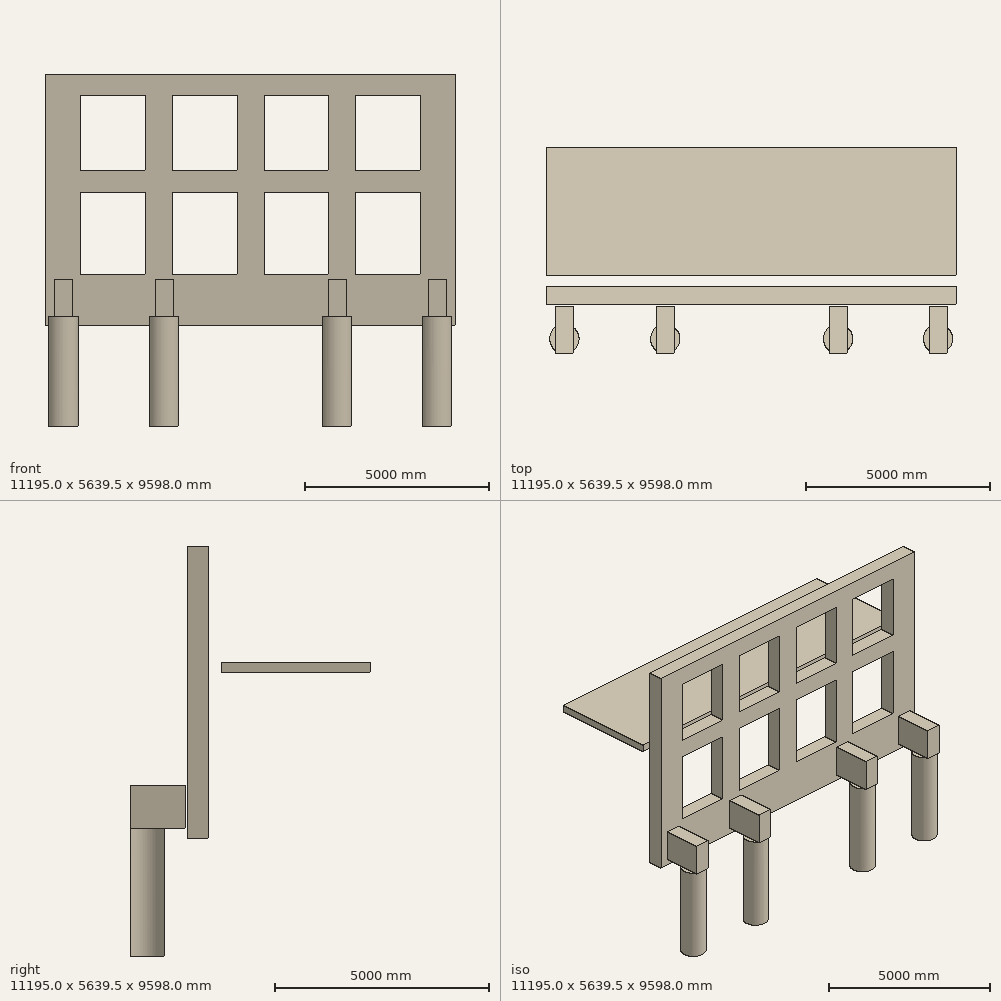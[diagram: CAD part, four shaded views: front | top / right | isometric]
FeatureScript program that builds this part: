
annotation { "Feature Type Name" : "Feature", "Feature Type Description" : "" }
export const myFeature = defineFeature(function(context is Context, id is Id, definition is map)
    precondition{}
    {
        {
            var Q0;
            Q0=qCreatedBy(makeId("Top.planeOp"),FACE);
            var sketch = newSketch(context, id + "F0", { "sketchPlane" : qUnion([Q0])});
            skLineSegment(sketch, "E0.bottom", {"start": v(2110, -40) * mm, "end": v(2610, -40) * mm});
            skLineSegment(sketch, "E0.top", {"start": v(2110, -1340) * mm, "end": v(2610, -1340) * mm});
            skLineSegment(sketch, "E0.left", {"start": v(2110, -40) * mm, "end": v(2110, -1340) * mm});
            skLineSegment(sketch, "E0.right", {"start": v(2610, -40) * mm, "end": v(2610, -1340) * mm});
            skLineSegment(sketch, "E1.bottom", {"start": v(4840, -40) * mm, "end": v(5340, -40) * mm});
            skLineSegment(sketch, "E1.top", {"start": v(4840, -1340) * mm, "end": v(5340, -1340) * mm});
            skLineSegment(sketch, "E1.left", {"start": v(4840, -40) * mm, "end": v(4840, -1340) * mm});
            skLineSegment(sketch, "E1.right", {"start": v(5340, -40) * mm, "end": v(5340, -1340) * mm});
            skLineSegment(sketch, "E2.bottom", {"start": v(-2110, -40) * mm, "end": v(-2610, -40) * mm});
            skLineSegment(sketch, "E2.top", {"start": v(-2110, -1340) * mm, "end": v(-2610, -1340) * mm});
            skLineSegment(sketch, "E2.left", {"start": v(-2110, -40) * mm, "end": v(-2110, -1340) * mm});
            skLineSegment(sketch, "E2.right", {"start": v(-2610, -40) * mm, "end": v(-2610, -1340) * mm});
            skLineSegment(sketch, "E3.bottom", {"start": v(-4865, -40) * mm, "end": v(-5365, -40) * mm});
            skLineSegment(sketch, "E3.top", {"start": v(-4865, -1340) * mm, "end": v(-5365, -1340) * mm});
            skLineSegment(sketch, "E3.left", {"start": v(-4865, -40) * mm, "end": v(-4865, -1340) * mm});
            skLineSegment(sketch, "E3.right", {"start": v(-5365, -40) * mm, "end": v(-5365, -1340) * mm});
            skSolve(sketch);
        }
        {
            var Q0;
            Q0=makeQuery(id+"F0.imprint","IMPRINT",FACE,{"disambiguationData":[TD([[makeQuery(id+"F0.imprint","IMPRINT",EDGE,{"derivedFrom":sQuery(id+"F0.wireOp",EDGE,"E3.bottom")}),1.0]])]});
            var Q1;
            Q1=makeQuery(id+"F0.imprint","IMPRINT",FACE,{"disambiguationData":[TD([[makeQuery(id+"F0.imprint","IMPRINT",EDGE,{"derivedFrom":sQuery(id+"F0.wireOp",EDGE,"E2.bottom")}),1.0]])]});
            var Q2;
            Q2=makeQuery(id+"F0.imprint","IMPRINT",FACE,{"disambiguationData":[TD([[makeQuery(id+"F0.imprint","IMPRINT",EDGE,{"derivedFrom":sQuery(id+"F0.wireOp",EDGE,"E0.bottom")}),-1.0]])]});
            var Q3;
            Q3=makeQuery(id+"F0.imprint","IMPRINT",FACE,{"disambiguationData":[TD([[makeQuery(id+"F0.imprint","IMPRINT",EDGE,{"derivedFrom":sQuery(id+"F0.wireOp",EDGE,"E1.bottom")}),-1.0]])]});
            extrude(context, id + "F1", {"entities" : qUnion([Q0, Q1, Q2, Q3]), "oppositeDirection" : true, "depth" : 1000 * mm});
        }
        {
            var Q0;
            Q0=makeQuery(id+"F1.opExtrude","CAP_FACE",FACE,{"disambiguationData":[OSD([sQuery(id+"F0.wireOp",EDGE,"E3.bottom"),sQuery(id+"F0.wireOp",EDGE,"E3.top"),sQuery(id+"F0.wireOp",EDGE,"E3.left"),sQuery(id+"F0.wireOp",EDGE,"E3.right")])],"isStart":false});
            var sketch = newSketch(context, id + "F2", { "sketchPlane" : qUnion([Q0])});
            skCircle(sketch, "E4", {"center": v(-5115, 940) * mm, "radius": 400 * mm});
            skPoint(sketch, "E4.centerSnap0", {"position": v(-5115, 40) * mm});
            skCircle(sketch, "E5", {"center": v(-2360, 940) * mm, "radius": 400 * mm});
            skCircle(sketch, "E6", {"center": v(2360, 940) * mm, "radius": 400 * mm});
            skCircle(sketch, "E7", {"center": v(5090, 940) * mm, "radius": 400 * mm});
            skSolve(sketch);
        }
        {
            var Q0;
            Q0=makeQuery(id+"F2.imprint","IMPRINT",FACE,{"disambiguationData":[TD([[makeQuery(id+"F2.imprint","IMPRINT",EDGE,{"derivedFrom":sQuery(id+"F2.wireOp",EDGE,"E5")}),1.0]])]});
            var Q1;
            Q1=makeQuery(id+"F2.imprint","IMPRINT",FACE,{"disambiguationData":[TD([[makeQuery(id+"F2.imprint","IMPRINT",EDGE,{"derivedFrom":sQuery(id+"F2.wireOp",EDGE,"E6")}),1.0]])]});
            var Q2;
            Q2=makeQuery(id+"F2.imprint","IMPRINT",FACE,{"disambiguationData":[TD([[makeQuery(id+"F2.imprint","IMPRINT",EDGE,{"derivedFrom":sQuery(id+"F2.wireOp",EDGE,"E7")}),1.0]])]});
            var Q3;
            {var subQ0=sQuery(id+"F2.wireOp",EDGE,"E4");var subQ1=makeQuery(id+"F1.opExtrude","CAP_EDGE",EDGE,{"disambiguationData":[OSD([sQuery(id+"F0.wireOp",EDGE,"E3.left")])],"isStart":false});var subQ2=makeQuery(id+"F2.imprint","INTERSECT",VERTEX,{"disambiguationData":[OD(0.0)],"derivedFrom":[subQ1,subQ0]});Q3=makeQuery(id+"F2.imprint","IMPRINT",FACE,{"disambiguationData":[TD([[makeQuery(id+"F2.imprint","IMPRINT",EDGE,{"disambiguationData":[TD([[subQ2,1.0]])],"derivedFrom":subQ0}),1.0]])]});}
            var Q4;
            {var subQ0=sQuery(id+"F2.wireOp",EDGE,"E4");var subQ6=makeQuery(id+"F2.imprint","INTERSECT",VERTEX,{"derivedFrom":[makeQuery(id+"F1.opExtrude","CAP_EDGE",EDGE,{"disambiguationData":[OSD([sQuery(id+"F0.wireOp",EDGE,"E3.top")])],"isStart":false}),subQ0]});Q4=makeQuery(id+"F2.imprint","IMPRINT",FACE,{"disambiguationData":[TD([[makeQuery(id+"F2.imprint","IMPRINT",EDGE,{"disambiguationData":[TD([[subQ6,1.0]])],"derivedFrom":subQ0}),1.0]])]});}
            var Q5;
            {var subQ0=sQuery(id+"F2.wireOp",EDGE,"E4");var subQ1=makeQuery(id+"F1.opExtrude","CAP_EDGE",EDGE,{"disambiguationData":[OSD([sQuery(id+"F0.wireOp",EDGE,"E3.right")])],"isStart":false});var subQ2=makeQuery(id+"F2.imprint","INTERSECT",VERTEX,{"disambiguationData":[OD(0.0)],"derivedFrom":[subQ1,subQ0]});Q5=makeQuery(id+"F2.imprint","IMPRINT",FACE,{"disambiguationData":[TD([[makeQuery(id+"F2.imprint","IMPRINT",EDGE,{"disambiguationData":[TD([[subQ2,-1.0]])],"derivedFrom":subQ0}),1.0]])]});}
            extrude(context, id + "F3", {"entities" : qUnion([Q0, Q1, Q2, Q3, Q4, Q5]), "operationType" : NewBodyOperationType.ADD, "depth" : 3000 * mm});
        }
        {
            var Q0;
            Q0=qCreatedBy(makeId("Front.planeOp"),FACE);
            var sketch = newSketch(context, id + "F4", { "sketchPlane" : qUnion([Q0])});
            skLineSegment(sketch, "E8.bottom", {"start": v(365, 150) * mm, "end": v(2135, 150) * mm});
            skLineSegment(sketch, "E8.top", {"start": v(365, 2395) * mm, "end": v(2135, 2395) * mm});
            skLineSegment(sketch, "E8.left", {"start": v(365, 150) * mm, "end": v(365, 2395) * mm});
            skLineSegment(sketch, "E8.right", {"start": v(2135, 150) * mm, "end": v(2135, 2395) * mm});
            skLineSegment(sketch, "E9.bottom", {"start": v(2870, 150) * mm, "end": v(4640, 150) * mm});
            skLineSegment(sketch, "E9.top", {"start": v(2870, 2395) * mm, "end": v(4640, 2395) * mm});
            skLineSegment(sketch, "E9.left", {"start": v(2870, 150) * mm, "end": v(2870, 2395) * mm});
            skLineSegment(sketch, "E9.right", {"start": v(4640, 150) * mm, "end": v(4640, 2395) * mm});
            skLineSegment(sketch, "E10.bottom", {"start": v(-365, 150) * mm, "end": v(-2140, 150) * mm});
            skLineSegment(sketch, "E10.top", {"start": v(-365, 2395) * mm, "end": v(-2140, 2395) * mm});
            skLineSegment(sketch, "E10.left", {"start": v(-365, 150) * mm, "end": v(-365, 2395) * mm});
            skLineSegment(sketch, "E10.right", {"start": v(-2140, 150) * mm, "end": v(-2140, 2395) * mm});
            skLineSegment(sketch, "E11.bottom", {"start": v(-2875, 150) * mm, "end": v(-4650, 150) * mm});
            skLineSegment(sketch, "E11.top", {"start": v(-2875, 2395) * mm, "end": v(-4650, 2395) * mm});
            skLineSegment(sketch, "E11.left", {"start": v(-2875, 150) * mm, "end": v(-2875, 2395) * mm});
            skLineSegment(sketch, "E11.right", {"start": v(-4650, 150) * mm, "end": v(-4650, 2395) * mm});
            skLineSegment(sketch, "E12.bottom", {"start": v(2870, 2988) * mm, "end": v(4640, 2988) * mm});
            skLineSegment(sketch, "E12.top", {"start": v(2870, 5018) * mm, "end": v(4640, 5018) * mm});
            skLineSegment(sketch, "E12.left", {"start": v(2870, 2988) * mm, "end": v(2870, 5018) * mm});
            skLineSegment(sketch, "E12.right", {"start": v(4640, 2988) * mm, "end": v(4640, 5018) * mm});
            skLineSegment(sketch, "E13.bottom", {"start": v(2135, 2988) * mm, "end": v(365, 2988) * mm});
            skLineSegment(sketch, "E13.top", {"start": v(2135, 5018) * mm, "end": v(365, 5018) * mm});
            skLineSegment(sketch, "E13.left", {"start": v(2135, 2988) * mm, "end": v(2135, 5018) * mm});
            skLineSegment(sketch, "E13.right", {"start": v(365, 2988) * mm, "end": v(365, 5018) * mm});
            skLineSegment(sketch, "E14.bottom", {"start": v(-365, 2988) * mm, "end": v(-2140, 2988) * mm});
            skLineSegment(sketch, "E14.top", {"start": v(-365, 5018) * mm, "end": v(-2140, 5018) * mm});
            skLineSegment(sketch, "E14.left", {"start": v(-365, 2988) * mm, "end": v(-365, 5018) * mm});
            skLineSegment(sketch, "E14.right", {"start": v(-2140, 2988) * mm, "end": v(-2140, 5018) * mm});
            skLineSegment(sketch, "E15.bottom", {"start": v(-2875, 2988) * mm, "end": v(-4650, 2988) * mm});
            skLineSegment(sketch, "E15.top", {"start": v(-2875, 5018) * mm, "end": v(-4650, 5018) * mm});
            skLineSegment(sketch, "E15.left", {"start": v(-2875, 2988) * mm, "end": v(-2875, 5018) * mm});
            skLineSegment(sketch, "E15.right", {"start": v(-4650, 2988) * mm, "end": v(-4650, 5018) * mm});
            skLineSegment(sketch, "E16.bottom", {"start": v(-5605, -1235.12) * mm, "end": v(5590, -1235.12) * mm});
            skLineSegment(sketch, "E16.top", {"start": v(-5605, 5598) * mm, "end": v(5590, 5598) * mm});
            skLineSegment(sketch, "E16.left", {"start": v(-5605, -1235.12) * mm, "end": v(-5605, 5598) * mm});
            skLineSegment(sketch, "E16.right", {"start": v(5590, -1235.12) * mm, "end": v(5590, 5598) * mm});
            skLineSegment(sketch, "E17", {"start": v(-5605, 5398) * mm, "end": v(5590, 5398) * mm, "construction": true});
            skPoint(sketch, "E18", {"position": v(-5605, 5398) * mm});
            skSolve(sketch);
        }
        {
            var Q0;
            Q0=qSketchRegion(id+"F4",true);
            extrude(context, id + "F5", {"entities" : qUnion([Q0]), "oppositeDirection" : true, "depth" : 500 * mm});
        }
        {
            var Q0;
            Q0=makeQuery(id+"F0.imprint","IMPRINT",FACE,{"disambiguationData":[TD([[makeQuery(id+"F0.imprint","IMPRINT",EDGE,{"derivedFrom":sQuery(id+"F0.wireOp",EDGE,"E3.bottom")}),1.0]])]});
            var sketch = newSketch(context, id + "F6", { "sketchPlane" : qUnion([Q0])});
            skLineSegment(sketch, "E19.0", {"start": v(-5605, 500) * mm, "end": v(5590, 500) * mm});
            skLineSegment(sketch, "E20", {"start": v(5590, 794.26) * mm, "end": v(-5605, 794.26) * mm});
            skLineSegment(sketch, "E21", {"start": v(-5605, 794.26) * mm, "end": v(-5605, 4299.47) * mm});
            skLineSegment(sketch, "E22", {"start": v(-5605, 4299.47) * mm, "end": v(5590, 4299.47) * mm});
            skLineSegment(sketch, "E23", {"start": v(5590, 4299.47) * mm, "end": v(5590, 794.26) * mm});
            skSolve(sketch);
        }
        {
            var Q0;
            Q0=makeQuery(id+"F6.imprint","IMPRINT",FACE,{"disambiguationData":[TD([[makeQuery(id+"F6.imprint","IMPRINT",EDGE,{"derivedFrom":sQuery(id+"F6.wireOp",EDGE,"E20")}),-1.0]])]});
            extrude(context, id + "F7", {"entities" : qUnion([Q0]), "depth" : (2642 + 240) * mm, "hasSecondDirection" : true, "secondDirectionOppositeDirection" : false, "secondDirectionDepth" : 2642 * mm});
        }
    });
